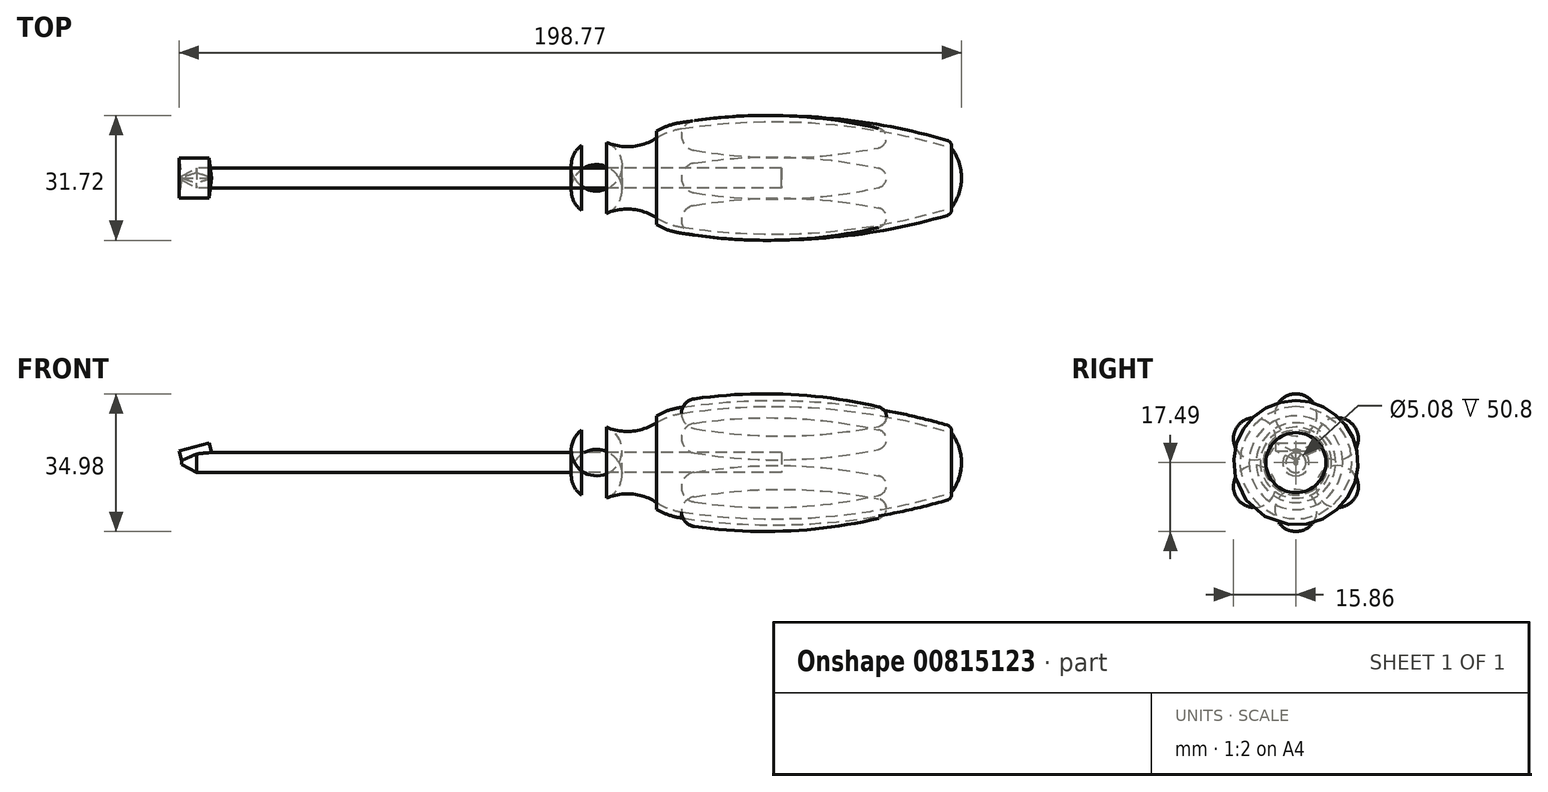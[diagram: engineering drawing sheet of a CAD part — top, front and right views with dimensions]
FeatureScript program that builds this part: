
annotation { "Feature Type Name" : "Feature", "Feature Type Description" : "" }
export const myFeature = defineFeature(function(context is Context, id is Id, definition is map)
    precondition{}
    {
        {
            var Q0;
            Q0=qCreatedBy(makeId("Front.planeOp"),FACE);
            var sketch = newSketch(context, id + "F0", { "sketchPlane" : qUnion([Q0])});
            skLineSegment(sketch, "E0", {"start": v(-101.6, 0) * mm, "end": v(96.52, 0) * mm});
            skLineSegment(sketch, "E1", {"start": v(96.52, 0) * mm, "end": v(117.55, 0) * mm, "construction": true});
            skLineSegment(sketch, "E2", {"start": v(50.8, 2.54) * mm, "end": v(-97.8, 2.54) * mm});
            skLineSegment(sketch, "E3", {"start": v(-101.6, 0.5) * mm, "end": v(-101.6, 0) * mm});
            skLineSegment(sketch, "E4", {"start": v(0, 2.54) * mm, "end": v(0, 8.25) * mm});
            skArc(sketch, "E5", {"start": v(6.35, 9.02) * mm, "mid": v(3.07, 9.48) * mm, "end": v(0, 8.25) * mm});
            skArc(sketch, "E6", {"start": v(6.35, 9.02) * mm, "mid": v(12.84, 7.99) * mm, "end": v(19.05, 10.11) * mm});
            skArc(sketch, "E7", {"start": v(25.4, 12.52) * mm, "mid": v(22.1, 11.65) * mm, "end": v(19.05, 10.11) * mm});
            skArc(sketch, "E8", {"start": v(93.98, 7.62) * mm, "mid": v(59.96, 13.9) * mm, "end": v(25.4, 12.52) * mm});
            skArc(sketch, "E9", {"start": v(96.52, 0) * mm, "mid": v(95.87, 4.02) * mm, "end": v(93.98, 7.62) * mm});
            skArc(sketch, "E10.0", {"start": v(25.17, 14.02) * mm, "mid": v(22.01, 13.24) * mm, "end": v(19.05, 11.9) * mm});
            skArc(sketch, "E10.1", {"start": v(92.95, 9.52) * mm, "mid": v(59.3, 15.46) * mm, "end": v(25.17, 14.02) * mm});
            skLineSegment(sketch, "E11", {"start": v(19.05, 11.9) * mm, "end": v(19.05, 10.11) * mm});
            skArc(sketch, "E12", {"start": v(93.98, 7.62) * mm, "mid": v(93.86, 8.78) * mm, "end": v(92.95, 9.52) * mm});
            skPoint(sketch, "E13.orphan", {"position": v(0, 0) * mm});
            skLineSegment(sketch, "E14", {"start": v(50.8, 2.54) * mm, "end": v(50.8, 0) * mm});
            skLineSegment(sketch, "E15", {"start": v(-101.6, 0.5) * mm, "end": v(-97.8, 2.54) * mm});
            skPoint(sketch, "E16.orphan", {"position": v(-101.6, 2.54) * mm});
            skSolve(sketch);
        }
        {
            var Q0;
            Q0=qCreatedBy(makeId("Front.planeOp"),FACE);
            var sketch = newSketch(context, id + "F1", { "sketchPlane" : qUnion([Q0])});
            skLineSegment(sketch, "E17", {"start": v(25.4, 12.52) * mm, "end": v(77.47, 11.64) * mm});
            skArc(sketch, "E18", {"start": v(28.67, 16.22) * mm, "mid": v(26.35, 14.97) * mm, "end": v(25.4, 12.52) * mm});
            skArc(sketch, "E19", {"start": v(77.47, 11.64) * mm, "mid": v(76.93, 13.25) * mm, "end": v(75.5, 14.16) * mm});
            skArc(sketch, "E20", {"start": v(75.5, 14.16) * mm, "mid": v(52.19, 17.37) * mm, "end": v(28.67, 16.22) * mm});
            skSolve(sketch);
        }
        {
            var Q0;
            Q0=qCreatedBy(makeId("Front.planeOp"),FACE);
            var sketch = newSketch(context, id + "F2", { "sketchPlane" : qUnion([Q0])});
            skLineSegment(sketch, "E21", {"start": v(-101.6, 0.5) * mm, "end": v(-93.98, 2.54) * mm});
            skSolve(sketch);
        }
        {
            var Q0;
            Q0=sQuery(id+"F2.wireOp",VERTEX,"E21.start");
            var Q1;
            Q1=sQuery(id+"F2.wireOp",EDGE,"E21");
            cPlane(context, id + "F3", {"entities" : qUnion([Q0, Q1]), "cplaneType" : CPlaneType.LINE_POINT, "offset" : 25.4 * mm, "width" : 152.4 * mm, "height" : 152.4 * mm});
        }
        {
            var Q0;
            Q0=qCreatedBy(id+"F3.planeOp",FACE);
            var sketch = newSketch(context, id + "F4", { "sketchPlane" : qUnion([Q0])});
            skLineSegment(sketch, "E22", {"start": v(5.08, 29.2) * mm, "end": v(0, 26.67) * mm});
            skLineSegment(sketch, "E23", {"start": v(0, 26.67) * mm, "end": v(-5.08, 29.2) * mm});
            skLineSegment(sketch, "E24", {"start": v(-5.08, 29.2) * mm, "end": v(5.08, 29.2) * mm});
            skLineSegment(sketch, "E25", {"start": v(0, 29.2) * mm, "end": v(0, 26.67) * mm, "construction": true});
            skSolve(sketch);
        }
        {
            var Q0;
            {var subQ0=sQuery(id+"F0.wireOp",EDGE,"E3");Q0=makeQuery(id+"F0.imprint","IMPRINT",FACE,{"disambiguationData":[TD([[makeQuery(id+"F0.imprint","IMPRINT",EDGE,{"derivedFrom":subQ0}),1.0]])]});}
            var Q1;
            Q1=sQuery(id+"F0.wireOp",EDGE,"E0");
            revolve(context, id + "F5", {"surfaceOperationType" : NewSurfaceOperationType.NEW, "entities" : qUnion([Q0]), "axis" : qUnion([Q1]), "revolveType" : RevolveType.FULL});
        }
        {
            var Q0;
            {var subQ0=sQuery(id+"F0.wireOp",EDGE,"E4");Q0=makeQuery(id+"F0.imprint","IMPRINT",FACE,{"disambiguationData":[TD([[makeQuery(id+"F0.imprint","IMPRINT",EDGE,{"derivedFrom":subQ0}),-1.0]])]});}
            var Q1;
            Q1=sQuery(id+"F0.wireOp",EDGE,"E1");
            revolve(context, id + "F6", {"surfaceOperationType" : NewSurfaceOperationType.NEW, "entities" : qUnion([Q0]), "axis" : qUnion([Q1]), "revolveType" : RevolveType.FULL});
        }
        {
            var Q0;
            Q0=makeQuery(id+"F0.imprint","IMPRINT",FACE,{"disambiguationData":[TD([[makeQuery(id+"F0.imprint","IMPRINT",EDGE,{"derivedFrom":sQuery(id+"F0.wireOp",EDGE,"E7")}),-1.0]])]});
            var Q1;
            Q1=sQuery(id+"F0.wireOp",EDGE,"E1");
            revolve(context, id + "F7", {"surfaceOperationType" : NewSurfaceOperationType.NEW, "entities" : qUnion([Q0]), "axis" : qUnion([Q1]), "revolveType" : RevolveType.FULL});
        }
        {
            var Q0;
            Q0=makeQuery(id+"F1.imprint","IMPRINT",FACE,{"disambiguationData":[TD([[makeQuery(id+"F1.imprint","IMPRINT",EDGE,{"derivedFrom":sQuery(id+"F1.wireOp",EDGE,"E17")}),1.0]])]});
            var Q1;
            Q1=sQuery(id+"F1.wireOp",EDGE,"E17");
            revolve(context, id + "F8", {"surfaceOperationType" : NewSurfaceOperationType.NEW, "entities" : qUnion([Q0]), "axis" : qUnion([Q1]), "revolveType" : RevolveType.FULL});
        }
        {
            var Q0;
            Q0=makeQuery(id+"F8.opRevolve","SWEPT_BODY",BODY,{"disambiguationData":[OSD([sQuery(id+"F1.wireOp",EDGE,"E17"),sQuery(id+"F1.wireOp",EDGE,"E18"),sQuery(id+"F1.wireOp",EDGE,"E19"),sQuery(id+"F1.wireOp",EDGE,"E20")])]});
            var Q1;
            Q1=sQuery(id+"F0.wireOp",EDGE,"E1");
            circularPattern(context, id + "F9", {"entities" : qUnion([Q0]), "axis" : qUnion([Q1]), "angle" : 360 * degree, "instanceCount" : 6, "equalSpace" : true});
        }
        {
            var Q0;
            Q0=makeQuery(id+"F4.imprint","IMPRINT",FACE,{"disambiguationData":[TD([[makeQuery(id+"F4.imprint","IMPRINT",EDGE,{"derivedFrom":sQuery(id+"F4.wireOp",EDGE,"E22")}),-1.0]])]});
            var Q1;
            Q1=sQuery(id+"F2.wireOp",EDGE,"E21");
            sweep(context, id + "F10", {"operationType" : NewBodyOperationType.REMOVE, "profiles" : qUnion([Q0]), "path" : qUnion([Q1])});
        }
        {
            var Q0;
            Q0=makeQuery(id+"F4.imprint","IMPRINT",FACE,{"disambiguationData":[TD([[makeQuery(id+"F4.imprint","IMPRINT",EDGE,{"derivedFrom":sQuery(id+"F4.wireOp",EDGE,"E22")}),-1.0]])]});
            var Q1;
            Q1=qConstructionFilter(qBodyType(qCreatedBy(id+"F2",EDGE),BodyType.WIRE),ConstructionObject.NO);
            sweep(context, id + "F11", {"profiles" : qUnion([Q0]), "path" : qUnion([Q1])});
        }
    });
